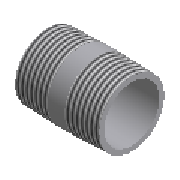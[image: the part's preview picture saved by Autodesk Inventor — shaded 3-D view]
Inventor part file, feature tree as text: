
AUTODESK INVENTOR PART (.ipt)
format: ipt  version: 2023.1 (Build 271208000, 208)  size: 187,392 bytes
history: native  units: mm (DEFAULTED — no unit token found)
features: other x6, revolve x1, sketch x1
ambient origin geometry x8: Origin, YZ Plane, XZ Plane, XY Plane, X Axis, Y Axis, Z Axis, Center Point
bodies: Solid1 (feature_tree)
feature tree (8):
  revolve  "Revolution1"  [1 undecoded]
  other  "Work Point3"
  other  "Work Point4"
  other  "Work Axis1"
  other  "Work Point5"
  other  "Work Axis2"
  other  "Work Point6"
  sketch  "Sketch1"  dims[d12=90.0deg d1=0.312398mm d2=38.0mm d3=17.1mm d4=0.0mm d5=17.1mm d6=0.0mm d7=9.53mm d8=26.441mm d57=21.6mm d60=14.53mm d62=0.0mm]
note: 1 required parameter value undecoded (feature->parameter linkage not recoverable at this tier; creation-order binding heuristic only, values carry confidence <= 0.55)
